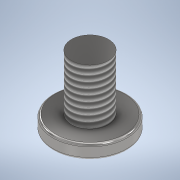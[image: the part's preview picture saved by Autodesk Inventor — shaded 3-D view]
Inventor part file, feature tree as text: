
AUTODESK INVENTOR PART (.ipt)
format: ipt  version: 2021 (Build 250183000, 183)  size: 134,144 bytes
history: native  units: mm
features: extrude x2, sketch x2, fillet x1, thread x1
ambient origin geometry x8: Origin, YZ Plane, XZ Plane, XY Plane, X Axis, Y Axis, Z Axis, Center Point
bodies: Solid1 (feature_tree)
feature tree (6):
  extrude  "Extrusion1"  Depth=3.0mm TaperAngle=0.0deg
  extrude  "Extrusion2"  Depth=12.0mm TaperAngle=0.0deg
  fillet  "Fillet1"  Radius=0.5mm
  thread  "Thread2"  [1 undecoded]
  sketch  "Sketch1"  dims[d0=16.0mm d1=3.0mm d2=0.0mm]
  sketch  "Sketch2"  dims[d3=8.0mm d4=12.0mm d5=0.0mm d8=0.5mm d9=12.0mm d10=0.0mm]
note: 1 required parameter value undecoded (feature->parameter linkage not recoverable at this tier; creation-order binding heuristic only, values carry confidence <= 0.55)
